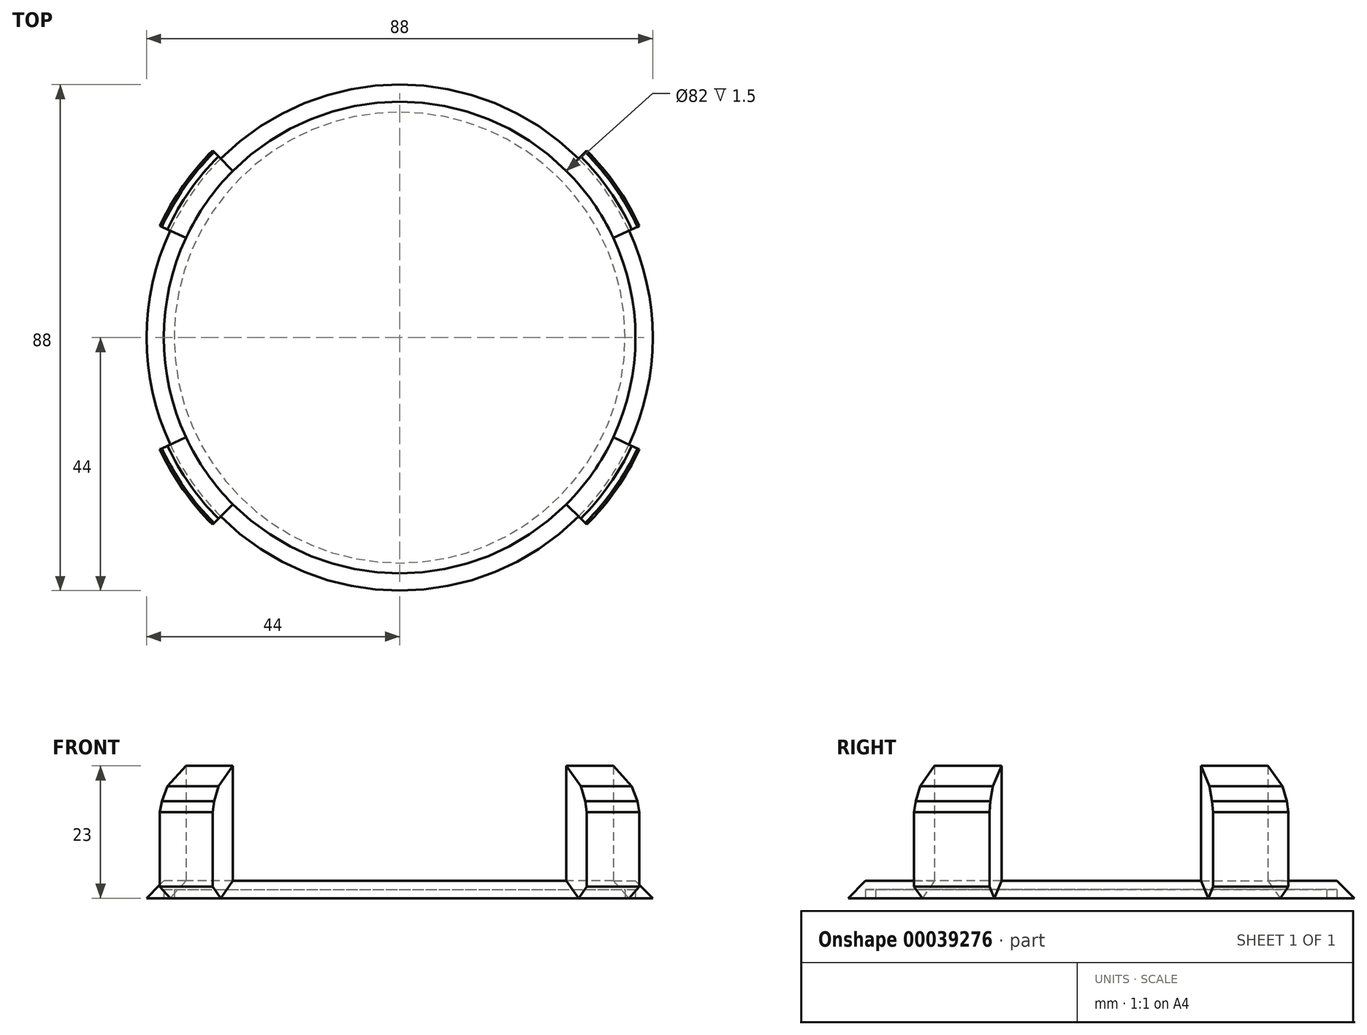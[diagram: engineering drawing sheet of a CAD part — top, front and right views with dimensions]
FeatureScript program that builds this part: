
annotation { "Feature Type Name" : "Feature", "Feature Type Description" : "" }
export const myFeature = defineFeature(function(context is Context, id is Id, definition is map)
    precondition{}
    {
        {
            var Q0;
            Q0=qCreatedBy(makeId("Top.planeOp"),FACE);
            var sketch = newSketch(context, id + "F0", { "sketchPlane" : qUnion([Q0])});
            skCircle(sketch, "E0", {"center": v(0, 0) * mm, "radius": 41 * mm});
            skCircle(sketch, "E1", {"center": v(0, 0) * mm, "radius": 46 * mm});
            skLineSegment(sketch, "E2", {"start": v(0, 41) * mm, "end": v(0, 46) * mm, "construction": true});
            skLineSegment(sketch, "E3", {"start": v(-29, 29) * mm, "end": v(-32.53, 32.53) * mm});
            skLineSegment(sketch, "E4", {"start": v(0, -41) * mm, "end": v(0, -46) * mm, "construction": true});
            skLineSegment(sketch, "E5", {"start": v(-29, -29) * mm, "end": v(-32.53, -32.53) * mm});
            skLineSegment(sketch, "E6.MirrorCS", {"start": v(29, 29) * mm, "end": v(32.53, 32.53) * mm});
            skLineSegment(sketch, "E7.MirrorCS", {"start": v(29, -29) * mm, "end": v(32.53, -32.53) * mm});
            skLineSegment(sketch, "E8", {"start": v(0, 0) * mm, "end": v(-41, 0) * mm, "construction": true});
            skLineSegment(sketch, "E9", {"start": v(-37.16, 17.33) * mm, "end": v(-41.7, 19.44) * mm});
            skLineSegment(sketch, "E10.MirrorCS", {"start": v(-37.16, -17.33) * mm, "end": v(-41.7, -19.44) * mm});
            skLineSegment(sketch, "E11.MirrorCS", {"start": v(37.16, -17.33) * mm, "end": v(41.7, -19.44) * mm});
            skLineSegment(sketch, "E12.MirrorCS", {"start": v(37.16, 17.33) * mm, "end": v(41.7, 19.44) * mm});
            skSolve(sketch);
        }
        {
            var Q0;
            {var subQ1=sQuery(id+"F0.wireOp",EDGE,"E3");Q0=makeQuery(id+"F0.imprint","IMPRINT",FACE,{"disambiguationData":[TD([[makeQuery(id+"F0.imprint","IMPRINT",EDGE,{"derivedFrom":subQ1}),1.0]])]});}
            var Q1;
            {var subQ1=sQuery(id+"F0.wireOp",EDGE,"E6.MirrorCS");Q1=makeQuery(id+"F0.imprint","IMPRINT",FACE,{"disambiguationData":[TD([[makeQuery(id+"F0.imprint","IMPRINT",EDGE,{"derivedFrom":subQ1}),-1.0]])]});}
            var Q2;
            {var subQ0=sQuery(id+"F0.wireOp",EDGE,"E5");Q2=makeQuery(id+"F0.imprint","IMPRINT",FACE,{"disambiguationData":[TD([[makeQuery(id+"F0.imprint","IMPRINT",EDGE,{"derivedFrom":subQ0}),-1.0]])]});}
            var Q3;
            {var subQ2=sQuery(id+"F0.wireOp",EDGE,"E7.MirrorCS");Q3=makeQuery(id+"F0.imprint","IMPRINT",FACE,{"disambiguationData":[TD([[makeQuery(id+"F0.imprint","IMPRINT",EDGE,{"derivedFrom":subQ2}),1.0]])]});}
            extrude(context, id + "F1", {"entities" : qUnion([Q0, Q1, Q2, Q3]), "depth" : 20 * mm});
        }
        {
            var Q0;
            {var subQ0=sQuery(id+"F0.wireOp",EDGE,"E1");Q0=makeQuery(id+"F1.opExtrude","CAP_EDGE",EDGE,{"disambiguationData":[OSD([subQ0]),TDD([makeQuery(id+"F0.imprint","IMPRINT",EDGE,{"disambiguationData":[TD([[makeQuery(id+"F0.imprint","INTERSECT",VERTEX,{"derivedFrom":[subQ0,sQuery(id+"F0.wireOp",EDGE,"E3")]}),-1.0]])],"derivedFrom":subQ0})])],"isStart":false});}
            var Q1;
            {var subQ0=sQuery(id+"F0.wireOp",EDGE,"E1");Q1=makeQuery(id+"F1.opExtrude","CAP_EDGE",EDGE,{"disambiguationData":[OSD([subQ0]),TDD([makeQuery(id+"F0.imprint","IMPRINT",EDGE,{"disambiguationData":[TD([[makeQuery(id+"F0.imprint","INTERSECT",VERTEX,{"derivedFrom":[subQ0,sQuery(id+"F0.wireOp",EDGE,"E6.MirrorCS")]}),1.0]])],"derivedFrom":subQ0})])],"isStart":false});}
            var Q2;
            {var subQ0=sQuery(id+"F0.wireOp",EDGE,"E1");Q2=makeQuery(id+"F1.opExtrude","CAP_EDGE",EDGE,{"disambiguationData":[OSD([subQ0]),TDD([makeQuery(id+"F0.imprint","IMPRINT",EDGE,{"disambiguationData":[TD([[makeQuery(id+"F0.imprint","INTERSECT",VERTEX,{"derivedFrom":[subQ0,sQuery(id+"F0.wireOp",EDGE,"E5")]}),1.0]])],"derivedFrom":subQ0})])],"isStart":false});}
            var Q3;
            {var subQ0=sQuery(id+"F0.wireOp",EDGE,"E1");Q3=makeQuery(id+"F1.opExtrude","CAP_EDGE",EDGE,{"disambiguationData":[OSD([subQ0]),TDD([makeQuery(id+"F0.imprint","IMPRINT",EDGE,{"disambiguationData":[TD([[makeQuery(id+"F0.imprint","INTERSECT",VERTEX,{"derivedFrom":[subQ0,sQuery(id+"F0.wireOp",EDGE,"E7.MirrorCS")]}),-1.0]])],"derivedFrom":subQ0})])],"isStart":false});}
            chamfer(context, id + "F2", {"entities" : qUnion([Q0, Q1, Q2, Q3]), "width" : 5 * mm, "tangentPropagation" : true});
        }
        {
            var Q0;
            {var subQ1=sQuery(id+"F0.wireOp",EDGE,"E3");Q0=makeQuery(id+"F0.imprint","IMPRINT",FACE,{"disambiguationData":[TD([[makeQuery(id+"F0.imprint","IMPRINT",EDGE,{"derivedFrom":subQ1}),1.0]])]});}
            var Q1;
            {var subQ1=sQuery(id+"F0.wireOp",EDGE,"E5");Q1=makeQuery(id+"F0.imprint","IMPRINT",FACE,{"disambiguationData":[TD([[makeQuery(id+"F0.imprint","IMPRINT",EDGE,{"derivedFrom":subQ1}),1.0]])]});}
            var Q2;
            {var subQ1=sQuery(id+"F0.wireOp",EDGE,"E6.MirrorCS");Q2=makeQuery(id+"F0.imprint","IMPRINT",FACE,{"disambiguationData":[TD([[makeQuery(id+"F0.imprint","IMPRINT",EDGE,{"derivedFrom":subQ1}),-1.0]])]});}
            var Q3;
            {var subQ1=sQuery(id+"F0.wireOp",EDGE,"E3");Q3=makeQuery(id+"F0.imprint","IMPRINT",FACE,{"disambiguationData":[TD([[makeQuery(id+"F0.imprint","IMPRINT",EDGE,{"derivedFrom":subQ1}),-1.0]])]});}
            var Q4;
            {var subQ0=sQuery(id+"F0.wireOp",EDGE,"E0");var subQ4=makeQuery(id+"F0.imprint","INTERSECT",VERTEX,{"derivedFrom":[subQ0,sQuery(id+"F0.wireOp",EDGE,"E3")]});Q4=makeQuery(id+"F0.imprint","IMPRINT",FACE,{"disambiguationData":[TD([[makeQuery(id+"F0.imprint","IMPRINT",EDGE,{"disambiguationData":[TD([[subQ4,1.0]])],"derivedFrom":subQ0}),1.0]])]});}
            var Q5;
            {var subQ0=sQuery(id+"F0.wireOp",EDGE,"E5");Q5=makeQuery(id+"F0.imprint","IMPRINT",FACE,{"disambiguationData":[TD([[makeQuery(id+"F0.imprint","IMPRINT",EDGE,{"derivedFrom":subQ0}),-1.0]])]});}
            var Q6;
            {var subQ2=sQuery(id+"F0.wireOp",EDGE,"E7.MirrorCS");Q6=makeQuery(id+"F0.imprint","IMPRINT",FACE,{"disambiguationData":[TD([[makeQuery(id+"F0.imprint","IMPRINT",EDGE,{"derivedFrom":subQ2}),1.0]])]});}
            var Q7;
            {var subQ2=sQuery(id+"F0.wireOp",EDGE,"E11.MirrorCS");Q7=makeQuery(id+"F0.imprint","IMPRINT",FACE,{"disambiguationData":[TD([[makeQuery(id+"F0.imprint","IMPRINT",EDGE,{"derivedFrom":subQ2}),1.0]])]});}
            var Q8;
            {var subQ1=sQuery(id+"F0.wireOp",EDGE,"E9");Q8=makeQuery(id+"F0.imprint","IMPRINT",FACE,{"disambiguationData":[TD([[makeQuery(id+"F0.imprint","IMPRINT",EDGE,{"derivedFrom":subQ1}),1.0]])]});}
            extrude(context, id + "F3", {"entities" : qUnion([Q0, Q1, Q2, Q3, Q4, Q5, Q6, Q7, Q8]), "operationType" : NewBodyOperationType.ADD, "oppositeDirection" : true, "depth" : 3 * mm});
        }
        {
            var Q0;
            {var subQ0=sQuery(id+"F0.wireOp",EDGE,"E1");var subQ1=makeQuery(id+"F0.imprint","IMPRINT",EDGE,{"disambiguationData":[TD([[makeQuery(id+"F0.imprint","INTERSECT",VERTEX,{"derivedFrom":[subQ0,sQuery(id+"F0.wireOp",EDGE,"E5")]}),1.0]])],"derivedFrom":subQ0});Q0=makeQuery(id+"F2.opChamfer","BLEND_EDGE",EDGE,{"blendedFrom":[makeQuery(id+"F1.opExtrude","CAP_EDGE",EDGE,{"disambiguationData":[OSD([subQ0]),TDD([subQ1])],"isStart":false}),makeQuery(id+"F1.opExtrude","SWEPT_FACE",FACE,{"disambiguationData":[OSD([subQ0]),TDD([subQ1])]})],"blendedInto":[makeQuery(id+"F1.opExtrude","SWEPT_FACE",FACE,{"disambiguationData":[OSD([subQ0]),TDD([subQ1])]})]});}
            var Q1;
            {var subQ0=sQuery(id+"F0.wireOp",EDGE,"E1");var subQ1=makeQuery(id+"F0.imprint","IMPRINT",EDGE,{"disambiguationData":[TD([[makeQuery(id+"F0.imprint","INTERSECT",VERTEX,{"derivedFrom":[subQ0,sQuery(id+"F0.wireOp",EDGE,"E3")]}),-1.0]])],"derivedFrom":subQ0});Q1=makeQuery(id+"F2.opChamfer","BLEND_EDGE",EDGE,{"blendedFrom":[makeQuery(id+"F1.opExtrude","CAP_EDGE",EDGE,{"disambiguationData":[OSD([subQ0]),TDD([subQ1])],"isStart":false}),makeQuery(id+"F1.opExtrude","SWEPT_FACE",FACE,{"disambiguationData":[OSD([subQ0]),TDD([subQ1])]})],"blendedInto":[makeQuery(id+"F1.opExtrude","SWEPT_FACE",FACE,{"disambiguationData":[OSD([subQ0]),TDD([subQ1])]})]});}
            var Q2;
            {var subQ0=sQuery(id+"F0.wireOp",EDGE,"E1");var subQ1=makeQuery(id+"F0.imprint","IMPRINT",EDGE,{"disambiguationData":[TD([[makeQuery(id+"F0.imprint","INTERSECT",VERTEX,{"derivedFrom":[subQ0,sQuery(id+"F0.wireOp",EDGE,"E7.MirrorCS")]}),-1.0]])],"derivedFrom":subQ0});Q2=makeQuery(id+"F2.opChamfer","BLEND_EDGE",EDGE,{"blendedFrom":[makeQuery(id+"F1.opExtrude","CAP_EDGE",EDGE,{"disambiguationData":[OSD([subQ0]),TDD([subQ1])],"isStart":false}),makeQuery(id+"F1.opExtrude","SWEPT_FACE",FACE,{"disambiguationData":[OSD([subQ0]),TDD([subQ1])]})],"blendedInto":[makeQuery(id+"F1.opExtrude","SWEPT_FACE",FACE,{"disambiguationData":[OSD([subQ0]),TDD([subQ1])]})]});}
            var Q3;
            {var subQ0=sQuery(id+"F0.wireOp",EDGE,"E1");var subQ1=makeQuery(id+"F0.imprint","IMPRINT",EDGE,{"disambiguationData":[TD([[makeQuery(id+"F0.imprint","INTERSECT",VERTEX,{"derivedFrom":[subQ0,sQuery(id+"F0.wireOp",EDGE,"E6.MirrorCS")]}),1.0]])],"derivedFrom":subQ0});Q3=makeQuery(id+"F2.opChamfer","BLEND_EDGE",EDGE,{"blendedFrom":[makeQuery(id+"F1.opExtrude","CAP_EDGE",EDGE,{"disambiguationData":[OSD([subQ0]),TDD([subQ1])],"isStart":false}),makeQuery(id+"F1.opExtrude","SWEPT_FACE",FACE,{"disambiguationData":[OSD([subQ0]),TDD([subQ1])]})],"blendedInto":[makeQuery(id+"F1.opExtrude","SWEPT_FACE",FACE,{"disambiguationData":[OSD([subQ0]),TDD([subQ1])]})]});}
            chamfer(context, id + "F4", {"entities" : qUnion([Q0, Q1, Q2, Q3]), "width" : 5 * mm, "tangentPropagation" : true});
        }
        {
            var Q0;
            Q0=makeQuery(id+"F3.opExtrude","CAP_FACE",FACE,{"disambiguationData":[OSD([sQuery(id+"F0.wireOp",EDGE,"E1")])],"isStart":false});
            var sketch = newSketch(context, id + "F5", { "sketchPlane" : qUnion([Q0])});
            skCircle(sketch, "E13", {"center": v(0, 0) * mm, "radius": 41 * mm});
            skCircle(sketch, "E14", {"center": v(0, 0) * mm, "radius": 39.2 * mm});
            skSolve(sketch);
        }
        {
            var Q0;
            Q0=makeQuery(id+"F5.imprint","IMPRINT",FACE,{"disambiguationData":[TD([[makeQuery(id+"F5.imprint","IMPRINT",EDGE,{"derivedFrom":sQuery(id+"F5.wireOp",EDGE,"E13")}),1.0]])]});
            extrude(context, id + "F6", {"entities" : qUnion([Q0]), "operationType" : NewBodyOperationType.REMOVE, "oppositeDirection" : true, "depth" : 1.5 * mm});
        }
        {
            var Q0;
            {var subQ0=sQuery(id+"F0.wireOp",EDGE,"E1");var subQ1=makeQuery(id+"F0.imprint","IMPRINT",EDGE,{"disambiguationData":[TD([[makeQuery(id+"F0.imprint","INTERSECT",VERTEX,{"derivedFrom":[subQ0,sQuery(id+"F0.wireOp",EDGE,"E5")]}),1.0]])],"derivedFrom":subQ0});var subQ2=makeQuery(id+"F1.opExtrude","SWEPT_FACE",FACE,{"disambiguationData":[OSD([subQ0]),TDD([subQ1])]});Q0=makeQuery(id+"F4.opChamfer","BLEND_EDGE",EDGE,{"blendedFrom":[makeQuery(id+"F2.opChamfer","BLEND_EDGE",EDGE,{"blendedFrom":[makeQuery(id+"F1.opExtrude","CAP_EDGE",EDGE,{"disambiguationData":[OSD([subQ0]),TDD([subQ1])],"isStart":false}),subQ2],"blendedInto":[subQ2]}),makeQuery(id+"F3.boolean.opBoolean","MERGE",FACE,{"derivedFrom":[makeQuery(id+"F1.opExtrude","SWEPT_FACE",FACE,{"disambiguationData":[OSD([subQ0]),TDD([makeQuery(id+"F0.imprint","IMPRINT",EDGE,{"disambiguationData":[TD([[makeQuery(id+"F0.imprint","INTERSECT",VERTEX,{"derivedFrom":[subQ0,sQuery(id+"F0.wireOp",EDGE,"E6.MirrorCS")]}),1.0]])],"derivedFrom":subQ0})])]}),makeQuery(id+"F1.opExtrude","SWEPT_FACE",FACE,{"disambiguationData":[OSD([subQ0]),TDD([makeQuery(id+"F0.imprint","IMPRINT",EDGE,{"disambiguationData":[TD([[makeQuery(id+"F0.imprint","INTERSECT",VERTEX,{"derivedFrom":[subQ0,sQuery(id+"F0.wireOp",EDGE,"E3")]}),-1.0]])],"derivedFrom":subQ0})])]}),subQ2,makeQuery(id+"F1.opExtrude","SWEPT_FACE",FACE,{"disambiguationData":[OSD([subQ0]),TDD([makeQuery(id+"F0.imprint","IMPRINT",EDGE,{"disambiguationData":[TD([[makeQuery(id+"F0.imprint","INTERSECT",VERTEX,{"derivedFrom":[subQ0,sQuery(id+"F0.wireOp",EDGE,"E7.MirrorCS")]}),-1.0]])],"derivedFrom":subQ0})])]}),makeQuery(id+"F3.opExtrude","SWEPT_FACE",FACE,{"disambiguationData":[OSD([subQ0])]})]})],"blendedInto":[makeQuery(id+"F3.boolean.opBoolean","MERGE",FACE,{"derivedFrom":[makeQuery(id+"F1.opExtrude","SWEPT_FACE",FACE,{"disambiguationData":[OSD([subQ0]),TDD([makeQuery(id+"F0.imprint","IMPRINT",EDGE,{"disambiguationData":[TD([[makeQuery(id+"F0.imprint","INTERSECT",VERTEX,{"derivedFrom":[subQ0,sQuery(id+"F0.wireOp",EDGE,"E6.MirrorCS")]}),1.0]])],"derivedFrom":subQ0})])]}),makeQuery(id+"F1.opExtrude","SWEPT_FACE",FACE,{"disambiguationData":[OSD([subQ0]),TDD([makeQuery(id+"F0.imprint","IMPRINT",EDGE,{"disambiguationData":[TD([[makeQuery(id+"F0.imprint","INTERSECT",VERTEX,{"derivedFrom":[subQ0,sQuery(id+"F0.wireOp",EDGE,"E3")]}),-1.0]])],"derivedFrom":subQ0})])]}),subQ2,makeQuery(id+"F1.opExtrude","SWEPT_FACE",FACE,{"disambiguationData":[OSD([subQ0]),TDD([makeQuery(id+"F0.imprint","IMPRINT",EDGE,{"disambiguationData":[TD([[makeQuery(id+"F0.imprint","INTERSECT",VERTEX,{"derivedFrom":[subQ0,sQuery(id+"F0.wireOp",EDGE,"E7.MirrorCS")]}),-1.0]])],"derivedFrom":subQ0})])]}),makeQuery(id+"F3.opExtrude","SWEPT_FACE",FACE,{"disambiguationData":[OSD([subQ0])]})]})]});}
            var Q1;
            {var subQ0=sQuery(id+"F0.wireOp",EDGE,"E1");var subQ1=makeQuery(id+"F0.imprint","IMPRINT",EDGE,{"disambiguationData":[TD([[makeQuery(id+"F0.imprint","INTERSECT",VERTEX,{"derivedFrom":[subQ0,sQuery(id+"F0.wireOp",EDGE,"E7.MirrorCS")]}),-1.0]])],"derivedFrom":subQ0});var subQ2=makeQuery(id+"F1.opExtrude","SWEPT_FACE",FACE,{"disambiguationData":[OSD([subQ0]),TDD([subQ1])]});Q1=makeQuery(id+"F4.opChamfer","BLEND_EDGE",EDGE,{"blendedFrom":[makeQuery(id+"F2.opChamfer","BLEND_EDGE",EDGE,{"blendedFrom":[makeQuery(id+"F1.opExtrude","CAP_EDGE",EDGE,{"disambiguationData":[OSD([subQ0]),TDD([subQ1])],"isStart":false}),subQ2],"blendedInto":[subQ2]}),makeQuery(id+"F3.boolean.opBoolean","MERGE",FACE,{"derivedFrom":[makeQuery(id+"F1.opExtrude","SWEPT_FACE",FACE,{"disambiguationData":[OSD([subQ0]),TDD([makeQuery(id+"F0.imprint","IMPRINT",EDGE,{"disambiguationData":[TD([[makeQuery(id+"F0.imprint","INTERSECT",VERTEX,{"derivedFrom":[subQ0,sQuery(id+"F0.wireOp",EDGE,"E6.MirrorCS")]}),1.0]])],"derivedFrom":subQ0})])]}),makeQuery(id+"F1.opExtrude","SWEPT_FACE",FACE,{"disambiguationData":[OSD([subQ0]),TDD([makeQuery(id+"F0.imprint","IMPRINT",EDGE,{"disambiguationData":[TD([[makeQuery(id+"F0.imprint","INTERSECT",VERTEX,{"derivedFrom":[subQ0,sQuery(id+"F0.wireOp",EDGE,"E3")]}),-1.0]])],"derivedFrom":subQ0})])]}),makeQuery(id+"F1.opExtrude","SWEPT_FACE",FACE,{"disambiguationData":[OSD([subQ0]),TDD([makeQuery(id+"F0.imprint","IMPRINT",EDGE,{"disambiguationData":[TD([[makeQuery(id+"F0.imprint","INTERSECT",VERTEX,{"derivedFrom":[subQ0,sQuery(id+"F0.wireOp",EDGE,"E5")]}),1.0]])],"derivedFrom":subQ0})])]}),subQ2,makeQuery(id+"F3.opExtrude","SWEPT_FACE",FACE,{"disambiguationData":[OSD([subQ0])]})]})],"blendedInto":[makeQuery(id+"F3.boolean.opBoolean","MERGE",FACE,{"derivedFrom":[makeQuery(id+"F1.opExtrude","SWEPT_FACE",FACE,{"disambiguationData":[OSD([subQ0]),TDD([makeQuery(id+"F0.imprint","IMPRINT",EDGE,{"disambiguationData":[TD([[makeQuery(id+"F0.imprint","INTERSECT",VERTEX,{"derivedFrom":[subQ0,sQuery(id+"F0.wireOp",EDGE,"E6.MirrorCS")]}),1.0]])],"derivedFrom":subQ0})])]}),makeQuery(id+"F1.opExtrude","SWEPT_FACE",FACE,{"disambiguationData":[OSD([subQ0]),TDD([makeQuery(id+"F0.imprint","IMPRINT",EDGE,{"disambiguationData":[TD([[makeQuery(id+"F0.imprint","INTERSECT",VERTEX,{"derivedFrom":[subQ0,sQuery(id+"F0.wireOp",EDGE,"E3")]}),-1.0]])],"derivedFrom":subQ0})])]}),makeQuery(id+"F1.opExtrude","SWEPT_FACE",FACE,{"disambiguationData":[OSD([subQ0]),TDD([makeQuery(id+"F0.imprint","IMPRINT",EDGE,{"disambiguationData":[TD([[makeQuery(id+"F0.imprint","INTERSECT",VERTEX,{"derivedFrom":[subQ0,sQuery(id+"F0.wireOp",EDGE,"E5")]}),1.0]])],"derivedFrom":subQ0})])]}),subQ2,makeQuery(id+"F3.opExtrude","SWEPT_FACE",FACE,{"disambiguationData":[OSD([subQ0])]})]})]});}
            var Q2;
            {var subQ0=sQuery(id+"F0.wireOp",EDGE,"E1");var subQ1=makeQuery(id+"F0.imprint","IMPRINT",EDGE,{"disambiguationData":[TD([[makeQuery(id+"F0.imprint","INTERSECT",VERTEX,{"derivedFrom":[subQ0,sQuery(id+"F0.wireOp",EDGE,"E6.MirrorCS")]}),1.0]])],"derivedFrom":subQ0});var subQ2=makeQuery(id+"F1.opExtrude","SWEPT_FACE",FACE,{"disambiguationData":[OSD([subQ0]),TDD([subQ1])]});Q2=makeQuery(id+"F4.opChamfer","BLEND_EDGE",EDGE,{"blendedFrom":[makeQuery(id+"F2.opChamfer","BLEND_EDGE",EDGE,{"blendedFrom":[makeQuery(id+"F1.opExtrude","CAP_EDGE",EDGE,{"disambiguationData":[OSD([subQ0]),TDD([subQ1])],"isStart":false}),subQ2],"blendedInto":[subQ2]}),makeQuery(id+"F3.boolean.opBoolean","MERGE",FACE,{"derivedFrom":[subQ2,makeQuery(id+"F1.opExtrude","SWEPT_FACE",FACE,{"disambiguationData":[OSD([subQ0]),TDD([makeQuery(id+"F0.imprint","IMPRINT",EDGE,{"disambiguationData":[TD([[makeQuery(id+"F0.imprint","INTERSECT",VERTEX,{"derivedFrom":[subQ0,sQuery(id+"F0.wireOp",EDGE,"E3")]}),-1.0]])],"derivedFrom":subQ0})])]}),makeQuery(id+"F1.opExtrude","SWEPT_FACE",FACE,{"disambiguationData":[OSD([subQ0]),TDD([makeQuery(id+"F0.imprint","IMPRINT",EDGE,{"disambiguationData":[TD([[makeQuery(id+"F0.imprint","INTERSECT",VERTEX,{"derivedFrom":[subQ0,sQuery(id+"F0.wireOp",EDGE,"E5")]}),1.0]])],"derivedFrom":subQ0})])]}),makeQuery(id+"F1.opExtrude","SWEPT_FACE",FACE,{"disambiguationData":[OSD([subQ0]),TDD([makeQuery(id+"F0.imprint","IMPRINT",EDGE,{"disambiguationData":[TD([[makeQuery(id+"F0.imprint","INTERSECT",VERTEX,{"derivedFrom":[subQ0,sQuery(id+"F0.wireOp",EDGE,"E7.MirrorCS")]}),-1.0]])],"derivedFrom":subQ0})])]}),makeQuery(id+"F3.opExtrude","SWEPT_FACE",FACE,{"disambiguationData":[OSD([subQ0])]})]})],"blendedInto":[makeQuery(id+"F3.boolean.opBoolean","MERGE",FACE,{"derivedFrom":[subQ2,makeQuery(id+"F1.opExtrude","SWEPT_FACE",FACE,{"disambiguationData":[OSD([subQ0]),TDD([makeQuery(id+"F0.imprint","IMPRINT",EDGE,{"disambiguationData":[TD([[makeQuery(id+"F0.imprint","INTERSECT",VERTEX,{"derivedFrom":[subQ0,sQuery(id+"F0.wireOp",EDGE,"E3")]}),-1.0]])],"derivedFrom":subQ0})])]}),makeQuery(id+"F1.opExtrude","SWEPT_FACE",FACE,{"disambiguationData":[OSD([subQ0]),TDD([makeQuery(id+"F0.imprint","IMPRINT",EDGE,{"disambiguationData":[TD([[makeQuery(id+"F0.imprint","INTERSECT",VERTEX,{"derivedFrom":[subQ0,sQuery(id+"F0.wireOp",EDGE,"E5")]}),1.0]])],"derivedFrom":subQ0})])]}),makeQuery(id+"F1.opExtrude","SWEPT_FACE",FACE,{"disambiguationData":[OSD([subQ0]),TDD([makeQuery(id+"F0.imprint","IMPRINT",EDGE,{"disambiguationData":[TD([[makeQuery(id+"F0.imprint","INTERSECT",VERTEX,{"derivedFrom":[subQ0,sQuery(id+"F0.wireOp",EDGE,"E7.MirrorCS")]}),-1.0]])],"derivedFrom":subQ0})])]}),makeQuery(id+"F3.opExtrude","SWEPT_FACE",FACE,{"disambiguationData":[OSD([subQ0])]})]})]});}
            var Q3;
            {var subQ0=sQuery(id+"F0.wireOp",EDGE,"E1");var subQ1=makeQuery(id+"F0.imprint","IMPRINT",EDGE,{"disambiguationData":[TD([[makeQuery(id+"F0.imprint","INTERSECT",VERTEX,{"derivedFrom":[subQ0,sQuery(id+"F0.wireOp",EDGE,"E3")]}),-1.0]])],"derivedFrom":subQ0});var subQ2=makeQuery(id+"F1.opExtrude","SWEPT_FACE",FACE,{"disambiguationData":[OSD([subQ0]),TDD([subQ1])]});Q3=makeQuery(id+"F4.opChamfer","BLEND_EDGE",EDGE,{"blendedFrom":[makeQuery(id+"F2.opChamfer","BLEND_EDGE",EDGE,{"blendedFrom":[makeQuery(id+"F1.opExtrude","CAP_EDGE",EDGE,{"disambiguationData":[OSD([subQ0]),TDD([subQ1])],"isStart":false}),subQ2],"blendedInto":[subQ2]}),makeQuery(id+"F3.boolean.opBoolean","MERGE",FACE,{"derivedFrom":[makeQuery(id+"F1.opExtrude","SWEPT_FACE",FACE,{"disambiguationData":[OSD([subQ0]),TDD([makeQuery(id+"F0.imprint","IMPRINT",EDGE,{"disambiguationData":[TD([[makeQuery(id+"F0.imprint","INTERSECT",VERTEX,{"derivedFrom":[subQ0,sQuery(id+"F0.wireOp",EDGE,"E6.MirrorCS")]}),1.0]])],"derivedFrom":subQ0})])]}),subQ2,makeQuery(id+"F1.opExtrude","SWEPT_FACE",FACE,{"disambiguationData":[OSD([subQ0]),TDD([makeQuery(id+"F0.imprint","IMPRINT",EDGE,{"disambiguationData":[TD([[makeQuery(id+"F0.imprint","INTERSECT",VERTEX,{"derivedFrom":[subQ0,sQuery(id+"F0.wireOp",EDGE,"E5")]}),1.0]])],"derivedFrom":subQ0})])]}),makeQuery(id+"F1.opExtrude","SWEPT_FACE",FACE,{"disambiguationData":[OSD([subQ0]),TDD([makeQuery(id+"F0.imprint","IMPRINT",EDGE,{"disambiguationData":[TD([[makeQuery(id+"F0.imprint","INTERSECT",VERTEX,{"derivedFrom":[subQ0,sQuery(id+"F0.wireOp",EDGE,"E7.MirrorCS")]}),-1.0]])],"derivedFrom":subQ0})])]}),makeQuery(id+"F3.opExtrude","SWEPT_FACE",FACE,{"disambiguationData":[OSD([subQ0])]})]})],"blendedInto":[makeQuery(id+"F3.boolean.opBoolean","MERGE",FACE,{"derivedFrom":[makeQuery(id+"F1.opExtrude","SWEPT_FACE",FACE,{"disambiguationData":[OSD([subQ0]),TDD([makeQuery(id+"F0.imprint","IMPRINT",EDGE,{"disambiguationData":[TD([[makeQuery(id+"F0.imprint","INTERSECT",VERTEX,{"derivedFrom":[subQ0,sQuery(id+"F0.wireOp",EDGE,"E6.MirrorCS")]}),1.0]])],"derivedFrom":subQ0})])]}),subQ2,makeQuery(id+"F1.opExtrude","SWEPT_FACE",FACE,{"disambiguationData":[OSD([subQ0]),TDD([makeQuery(id+"F0.imprint","IMPRINT",EDGE,{"disambiguationData":[TD([[makeQuery(id+"F0.imprint","INTERSECT",VERTEX,{"derivedFrom":[subQ0,sQuery(id+"F0.wireOp",EDGE,"E5")]}),1.0]])],"derivedFrom":subQ0})])]}),makeQuery(id+"F1.opExtrude","SWEPT_FACE",FACE,{"disambiguationData":[OSD([subQ0]),TDD([makeQuery(id+"F0.imprint","IMPRINT",EDGE,{"disambiguationData":[TD([[makeQuery(id+"F0.imprint","INTERSECT",VERTEX,{"derivedFrom":[subQ0,sQuery(id+"F0.wireOp",EDGE,"E7.MirrorCS")]}),-1.0]])],"derivedFrom":subQ0})])]}),makeQuery(id+"F3.opExtrude","SWEPT_FACE",FACE,{"disambiguationData":[OSD([subQ0])]})]})]});}
            chamfer(context, id + "F7", {"entities" : qUnion([Q0, Q1, Q2, Q3]), "width" : 5 * mm, "tangentPropagation" : true});
        }
        {
            var Q0;
            {var subQ0=sQuery(id+"F0.wireOp",EDGE,"E1");var subQ1=makeQuery(id+"F0.imprint","IMPRINT",EDGE,{"disambiguationData":[TD([[makeQuery(id+"F0.imprint","INTERSECT",VERTEX,{"derivedFrom":[subQ0,sQuery(id+"F0.wireOp",EDGE,"E6.MirrorCS")]}),1.0]])],"derivedFrom":subQ0});var subQ2=makeQuery(id+"F1.opExtrude","SWEPT_FACE",FACE,{"disambiguationData":[OSD([subQ0]),TDD([subQ1])]});Q0=makeQuery(id+"F7.opChamfer","BLEND_EDGE",EDGE,{"blendedFrom":[makeQuery(id+"F2.opChamfer","BLEND_EDGE",EDGE,{"blendedFrom":[makeQuery(id+"F1.opExtrude","CAP_EDGE",EDGE,{"disambiguationData":[OSD([subQ0]),TDD([subQ1])],"isStart":false}),subQ2],"blendedInto":[subQ2]}),makeQuery(id+"F4.opChamfer","SPLIT",FACE,{"disambiguationData":[OD(1.0)],"derivedFrom":makeQuery(id+"F3.boolean.opBoolean","MERGE",FACE,{"derivedFrom":[makeQuery(id+"F1.opExtrude","SWEPT_FACE",FACE,{"disambiguationData":[OSD([subQ0]),TDD([makeQuery(id+"F0.imprint","IMPRINT",EDGE,{"disambiguationData":[TD([[makeQuery(id+"F0.imprint","INTERSECT",VERTEX,{"derivedFrom":[subQ0,sQuery(id+"F0.wireOp",EDGE,"E3")]}),-1.0]])],"derivedFrom":subQ0})])]}),subQ2,makeQuery(id+"F3.opExtrude","SWEPT_FACE",FACE,{"disambiguationData":[OSD([subQ0])]})]})})],"blendedInto":[makeQuery(id+"F4.opChamfer","SPLIT",FACE,{"disambiguationData":[OD(1.0)],"derivedFrom":makeQuery(id+"F3.boolean.opBoolean","MERGE",FACE,{"derivedFrom":[makeQuery(id+"F1.opExtrude","SWEPT_FACE",FACE,{"disambiguationData":[OSD([subQ0]),TDD([makeQuery(id+"F0.imprint","IMPRINT",EDGE,{"disambiguationData":[TD([[makeQuery(id+"F0.imprint","INTERSECT",VERTEX,{"derivedFrom":[subQ0,sQuery(id+"F0.wireOp",EDGE,"E3")]}),-1.0]])],"derivedFrom":subQ0})])]}),subQ2,makeQuery(id+"F3.opExtrude","SWEPT_FACE",FACE,{"disambiguationData":[OSD([subQ0])]})]})})]});}
            var Q1;
            {var subQ0=sQuery(id+"F0.wireOp",EDGE,"E1");var subQ1=makeQuery(id+"F0.imprint","IMPRINT",EDGE,{"disambiguationData":[TD([[makeQuery(id+"F0.imprint","INTERSECT",VERTEX,{"derivedFrom":[subQ0,sQuery(id+"F0.wireOp",EDGE,"E3")]}),-1.0]])],"derivedFrom":subQ0});var subQ2=makeQuery(id+"F1.opExtrude","SWEPT_FACE",FACE,{"disambiguationData":[OSD([subQ0]),TDD([subQ1])]});Q1=makeQuery(id+"F7.opChamfer","BLEND_EDGE",EDGE,{"blendedFrom":[makeQuery(id+"F2.opChamfer","BLEND_EDGE",EDGE,{"blendedFrom":[makeQuery(id+"F1.opExtrude","CAP_EDGE",EDGE,{"disambiguationData":[OSD([subQ0]),TDD([subQ1])],"isStart":false}),subQ2],"blendedInto":[subQ2]}),makeQuery(id+"F4.opChamfer","SPLIT",FACE,{"disambiguationData":[OD(0.0)],"derivedFrom":makeQuery(id+"F3.boolean.opBoolean","MERGE",FACE,{"derivedFrom":[subQ2,makeQuery(id+"F1.opExtrude","SWEPT_FACE",FACE,{"disambiguationData":[OSD([subQ0]),TDD([makeQuery(id+"F0.imprint","IMPRINT",EDGE,{"disambiguationData":[TD([[makeQuery(id+"F0.imprint","INTERSECT",VERTEX,{"derivedFrom":[subQ0,sQuery(id+"F0.wireOp",EDGE,"E6.MirrorCS")]}),1.0]])],"derivedFrom":subQ0})])]}),makeQuery(id+"F3.opExtrude","SWEPT_FACE",FACE,{"disambiguationData":[OSD([subQ0])]})]})})],"blendedInto":[makeQuery(id+"F4.opChamfer","SPLIT",FACE,{"disambiguationData":[OD(0.0)],"derivedFrom":makeQuery(id+"F3.boolean.opBoolean","MERGE",FACE,{"derivedFrom":[subQ2,makeQuery(id+"F1.opExtrude","SWEPT_FACE",FACE,{"disambiguationData":[OSD([subQ0]),TDD([makeQuery(id+"F0.imprint","IMPRINT",EDGE,{"disambiguationData":[TD([[makeQuery(id+"F0.imprint","INTERSECT",VERTEX,{"derivedFrom":[subQ0,sQuery(id+"F0.wireOp",EDGE,"E6.MirrorCS")]}),1.0]])],"derivedFrom":subQ0})])]}),makeQuery(id+"F3.opExtrude","SWEPT_FACE",FACE,{"disambiguationData":[OSD([subQ0])]})]})})]});}
            var Q2;
            {var subQ0=sQuery(id+"F0.wireOp",EDGE,"E1");var subQ2=sQuery(id+"F0.wireOp",EDGE,"E3");Q2=makeQuery(id+"F3.boolean.opBoolean","SPLIT",EDGE,{"disambiguationData":[TD([makeQuery(id+"F1.opExtrude","SWEPT_FACE",FACE,{"disambiguationData":[OSD([subQ2])]})])],"derivedFrom":makeQuery(id+"F3.opExtrude","CAP_EDGE",EDGE,{"disambiguationData":[OSD([subQ0])],"isStart":true})});}
            var Q3;
            {var subQ0=sQuery(id+"F0.wireOp",EDGE,"E1");var subQ2=sQuery(id+"F0.wireOp",EDGE,"E5");Q3=makeQuery(id+"F3.boolean.opBoolean","SPLIT",EDGE,{"disambiguationData":[TD([makeQuery(id+"F1.opExtrude","SWEPT_FACE",FACE,{"disambiguationData":[OSD([subQ2])]})])],"derivedFrom":makeQuery(id+"F3.opExtrude","CAP_EDGE",EDGE,{"disambiguationData":[OSD([subQ0])],"isStart":true})});}
            var Q4;
            {var subQ0=sQuery(id+"F0.wireOp",EDGE,"E1");var subQ1=sQuery(id+"F0.wireOp",EDGE,"E9");Q4=makeQuery(id+"F3.boolean.opBoolean","SPLIT",EDGE,{"disambiguationData":[TD([makeQuery(id+"F1.opExtrude","SWEPT_FACE",FACE,{"disambiguationData":[OSD([subQ1])]})])],"derivedFrom":makeQuery(id+"F3.opExtrude","CAP_EDGE",EDGE,{"disambiguationData":[OSD([subQ0])],"isStart":true})});}
            var Q5;
            {var subQ0=sQuery(id+"F0.wireOp",EDGE,"E1");var subQ1=sQuery(id+"F0.wireOp",EDGE,"E11.MirrorCS");Q5=makeQuery(id+"F3.boolean.opBoolean","SPLIT",EDGE,{"disambiguationData":[TD([makeQuery(id+"F1.opExtrude","SWEPT_FACE",FACE,{"disambiguationData":[OSD([subQ1])]})])],"derivedFrom":makeQuery(id+"F3.opExtrude","CAP_EDGE",EDGE,{"disambiguationData":[OSD([subQ0])],"isStart":true})});}
            chamfer(context, id + "F8", {"entities" : qUnion([Q0, Q1, Q2, Q3, Q4, Q5]), "width" : 5 * mm, "tangentPropagation" : true});
        }
        {
            var Q0;
            Q0=makeQuery(id+"F3.opExtrude","CAP_EDGE",EDGE,{"disambiguationData":[OSD([sQuery(id+"F0.wireOp",EDGE,"E1")])],"isStart":false});
            chamfer(context, id + "F9", {"entities" : qUnion([Q0]), "width" : 2 * mm, "tangentPropagation" : true});
        }
    });
